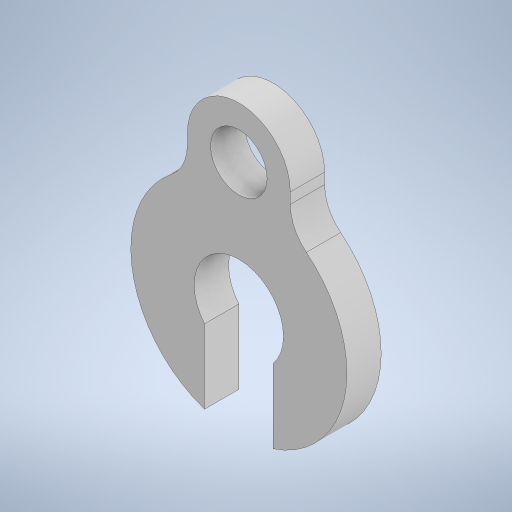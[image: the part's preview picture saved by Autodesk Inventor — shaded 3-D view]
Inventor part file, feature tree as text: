
AUTODESK INVENTOR PART (.ipt)
format: ipt  version: 2024 (Build 280153000, 153)  size: 257,536 bytes
history: native  units: in
note: dims shown in document units (in); Inventor stores cm internally (conversion verified against a paired STEP export)
features: extrude x1, fillet x1, sketch x1
ambient origin geometry x8: Origin, YZ Plane, XZ Plane, XY Plane, X Axis, Y Axis, Z Axis, Center Point
bodies: Solid1 (feature_tree)
feature tree (3):
  extrude  "Extrusion1"  Depth=0.0625in
  fillet  "Fillet1"  Radius=0.0825in
  sketch  "Sketch1"  dims[d0=0.315in d1=0.13in d2=0.0825in d3=0.1in d4=0.1875in d5=0.15in d7=0.075in d8=0.15in d9=0.049in d10=0.1575in d11=0.1575in d12=0.049in d13=0.05in d14=0.0in d15=0.0625in]
